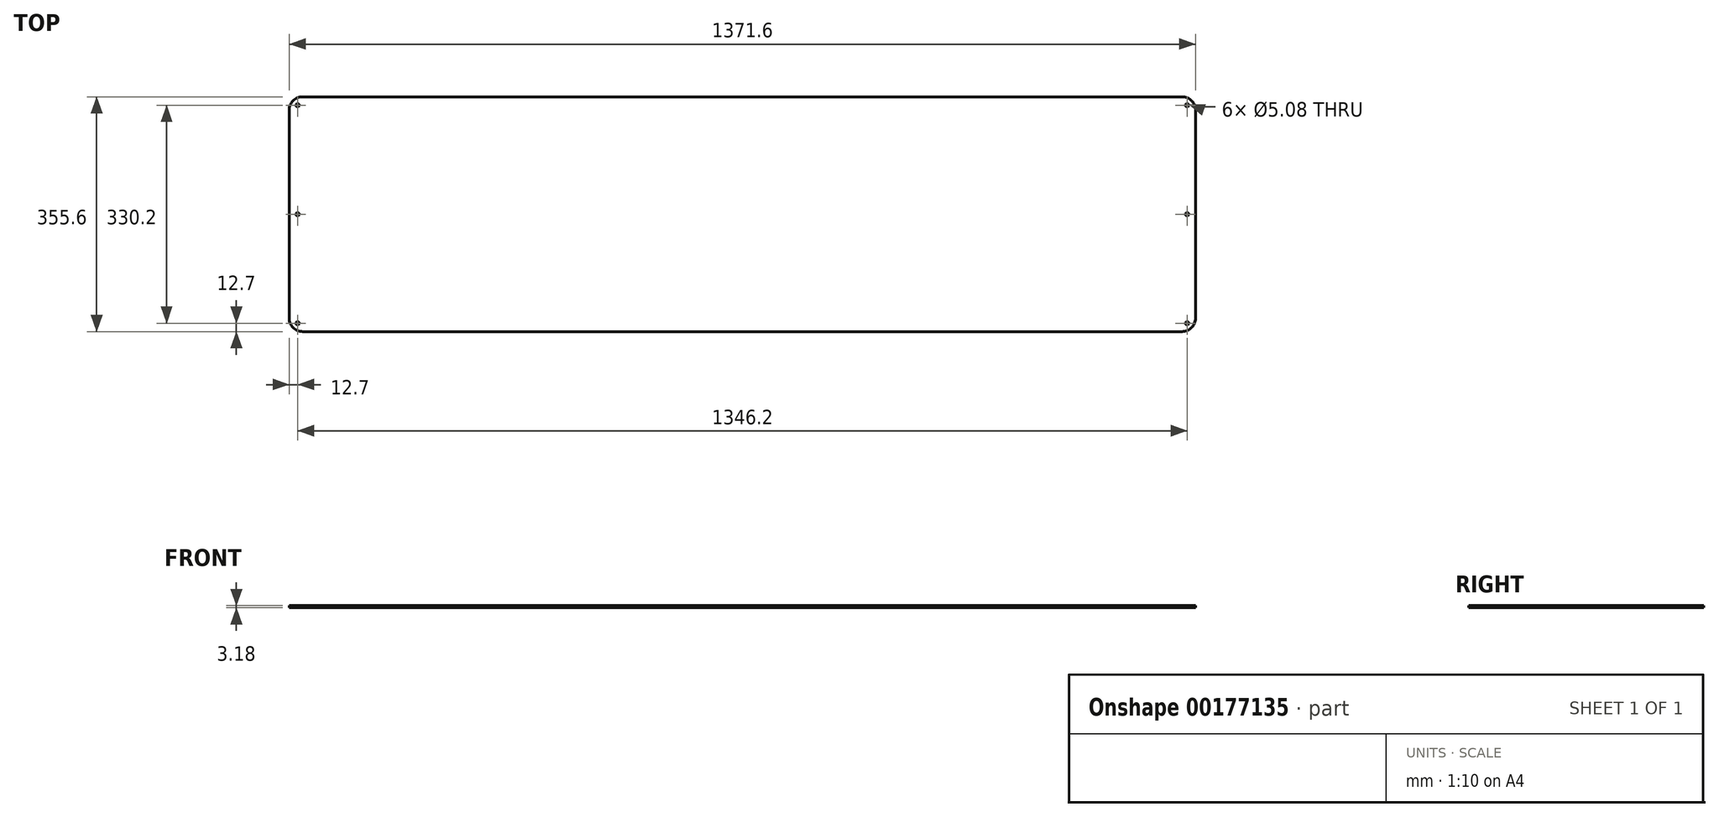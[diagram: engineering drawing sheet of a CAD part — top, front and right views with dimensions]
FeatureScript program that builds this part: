
annotation { "Feature Type Name" : "Feature", "Feature Type Description" : "" }
export const myFeature = defineFeature(function(context is Context, id is Id, definition is map)
    precondition{}
    {
        {
            var Q0;
            Q0=qCreatedBy(makeId("Top.planeOp"),FACE);
            var sketch = newSketch(context, id + "F0", { "sketchPlane" : qUnion([Q0])});
            skLineSegment(sketch, "E0.bottom", {"start": v(0, 0) * mm, "end": v(1371.6, 0) * mm});
            skLineSegment(sketch, "E0.top", {"start": v(0, 355.6) * mm, "end": v(1371.6, 355.6) * mm});
            skLineSegment(sketch, "E0.left", {"start": v(0, 0) * mm, "end": v(0, 355.6) * mm});
            skLineSegment(sketch, "E0.right", {"start": v(1371.6, 0) * mm, "end": v(1371.6, 355.6) * mm});
            skCircle(sketch, "E1", {"center": v(12.7, 342.9) * mm, "radius": 2.54 * mm});
            skCircle(sketch, "E2", {"center": v(12.7, 12.7) * mm, "radius": 2.54 * mm});
            skCircle(sketch, "E3", {"center": v(1358.9, 12.7) * mm, "radius": 2.54 * mm});
            skCircle(sketch, "E4", {"center": v(1358.9, 342.9) * mm, "radius": 2.54 * mm});
            skCircle(sketch, "E5", {"center": v(12.7, 177.8) * mm, "radius": 2.54 * mm});
            skCircle(sketch, "E6", {"center": v(1358.9, 177.8) * mm, "radius": 2.54 * mm});
            skSolve(sketch);
        }
        {
            var Q0;
            Q0=makeQuery(id+"F0.imprint","IMPRINT",FACE,{"disambiguationData":[TD([[makeQuery(id+"F0.imprint","IMPRINT",EDGE,{"derivedFrom":sQuery(id+"F0.wireOp",EDGE,"E0.bottom")}),1.0]])]});
            extrude(context, id + "F1", {"entities" : qUnion([Q0]), "depth" : 3.17 * mm});
        }
        {
            var Q0;
            Q0=makeQuery(id+"F1.opExtrude","SWEPT_EDGE",EDGE,{"disambiguationData":[OSD([sQuery(id+"F0.wireOp",EDGE,"E0.top"),sQuery(id+"F0.wireOp",EDGE,"E0.left")])]});
            var Q1;
            Q1=makeQuery(id+"F1.opExtrude","SWEPT_EDGE",EDGE,{"disambiguationData":[OSD([sQuery(id+"F0.wireOp",EDGE,"E0.bottom"),sQuery(id+"F0.wireOp",EDGE,"E0.left")])]});
            var Q2;
            Q2=makeQuery(id+"F1.opExtrude","SWEPT_EDGE",EDGE,{"disambiguationData":[OSD([sQuery(id+"F0.wireOp",EDGE,"E0.bottom"),sQuery(id+"F0.wireOp",EDGE,"E0.right")])]});
            var Q3;
            Q3=makeQuery(id+"F1.opExtrude","SWEPT_EDGE",EDGE,{"disambiguationData":[OSD([sQuery(id+"F0.wireOp",EDGE,"E0.top"),sQuery(id+"F0.wireOp",EDGE,"E0.right")])]});
            fillet(context, id + "F2", {"entities" : qUnion([Q0, Q1, Q2, Q3]), "radius" : 20.32 * mm, "tangentPropagation" : true, "allowEdgeOverflow" : false});
        }
    });
